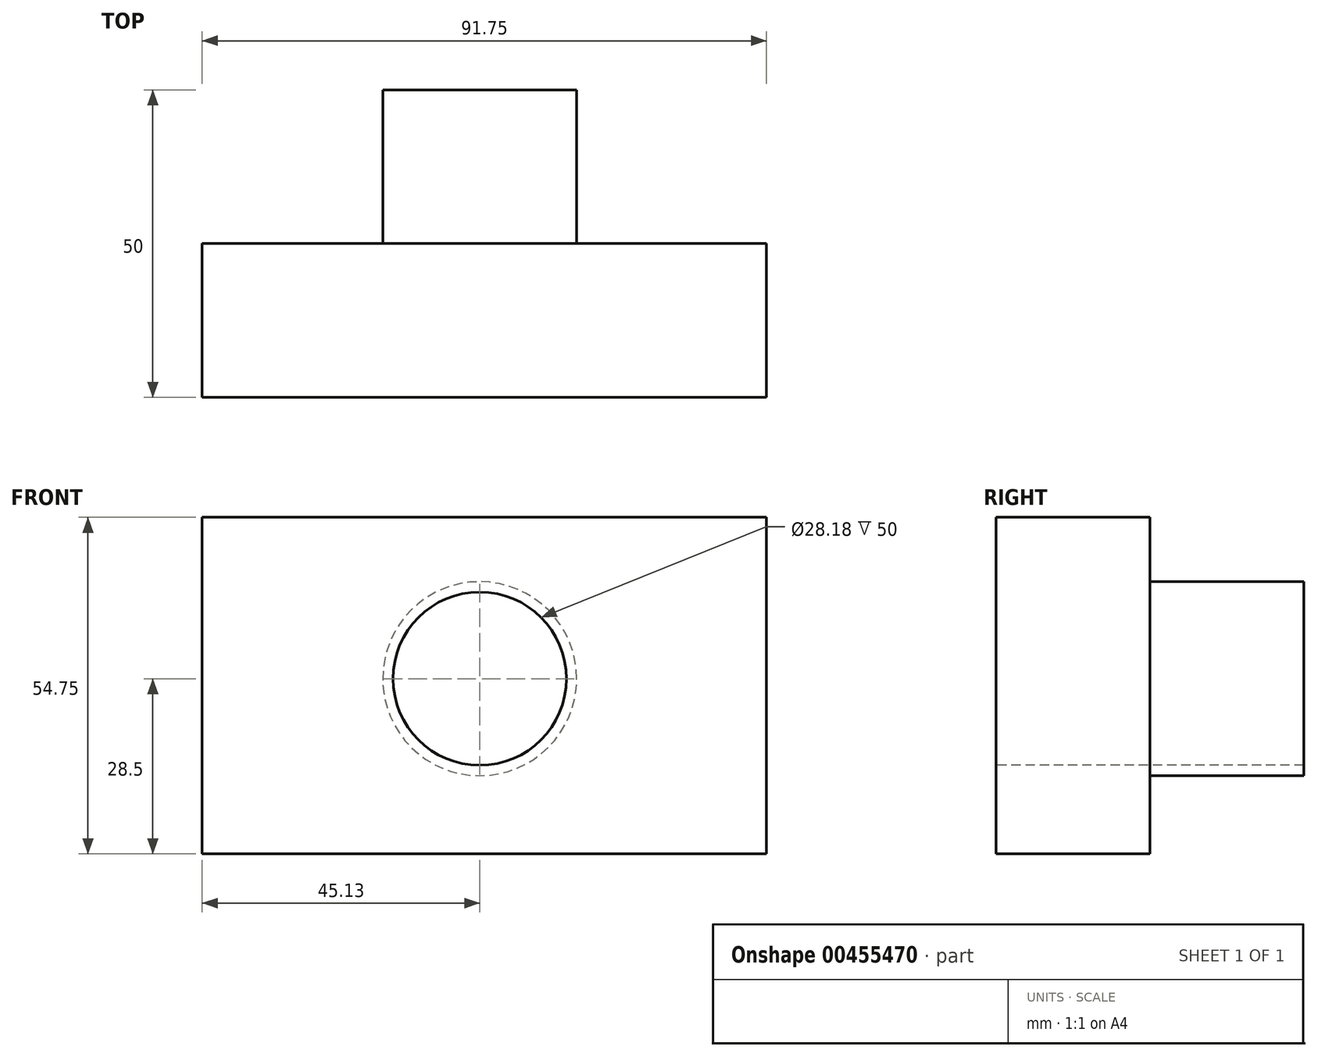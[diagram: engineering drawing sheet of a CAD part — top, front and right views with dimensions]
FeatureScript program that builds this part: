
annotation { "Feature Type Name" : "Feature", "Feature Type Description" : "" }
export const myFeature = defineFeature(function(context is Context, id is Id, definition is map)
    precondition{}
    {
        {
            var Q0;
            Q0=qCreatedBy(makeId("Front.planeOp"),FACE);
            var sketch = newSketch(context, id + "F0", { "sketchPlane" : qUnion([Q0])});
            skLineSegment(sketch, "E0.bottom", {"start": v(-45.13, 20.25) * mm, "end": v(46.62, 20.25) * mm});
            skLineSegment(sketch, "E0.top", {"start": v(-45.13, -34.5) * mm, "end": v(46.62, -34.5) * mm});
            skLineSegment(sketch, "E0.left", {"start": v(-45.13, 20.25) * mm, "end": v(-45.13, -34.5) * mm});
            skLineSegment(sketch, "E0.right", {"start": v(46.62, 20.25) * mm, "end": v(46.62, -34.5) * mm});
            skCircle(sketch, "E1", {"center": v(0, -6) * mm, "radius": 15.77 * mm});
            skCircle(sketch, "E2", {"center": v(0, -6) * mm, "radius": 14.1 * mm});
            skSolve(sketch);
        }
        {
            var Q0;
            Q0=makeQuery(id+"F0.imprint","IMPRINT",FACE,{"disambiguationData":[TD([[makeQuery(id+"F0.imprint","IMPRINT",EDGE,{"derivedFrom":sQuery(id+"F0.wireOp",EDGE,"E0.bottom")}),-1.0]])]});
            extrude(context, id + "F1", {"entities" : qUnion([Q0]), "depth" : 25 * mm});
        }
        {
            var Q0;
            Q0=makeQuery(id+"F0.imprint","IMPRINT",FACE,{"disambiguationData":[TD([[makeQuery(id+"F0.imprint","IMPRINT",EDGE,{"derivedFrom":sQuery(id+"F0.wireOp",EDGE,"E1")}),1.0]])]});
            extrude(context, id + "F2", {"entities" : qUnion([Q0]), "operationType" : NewBodyOperationType.ADD, "oppositeDirection" : true, "depth" : 25 * mm, "hasSecondDirection" : true, "secondDirectionOppositeDirection" : false, "secondDirectionDepth" : 25 * mm});
        }
    });
